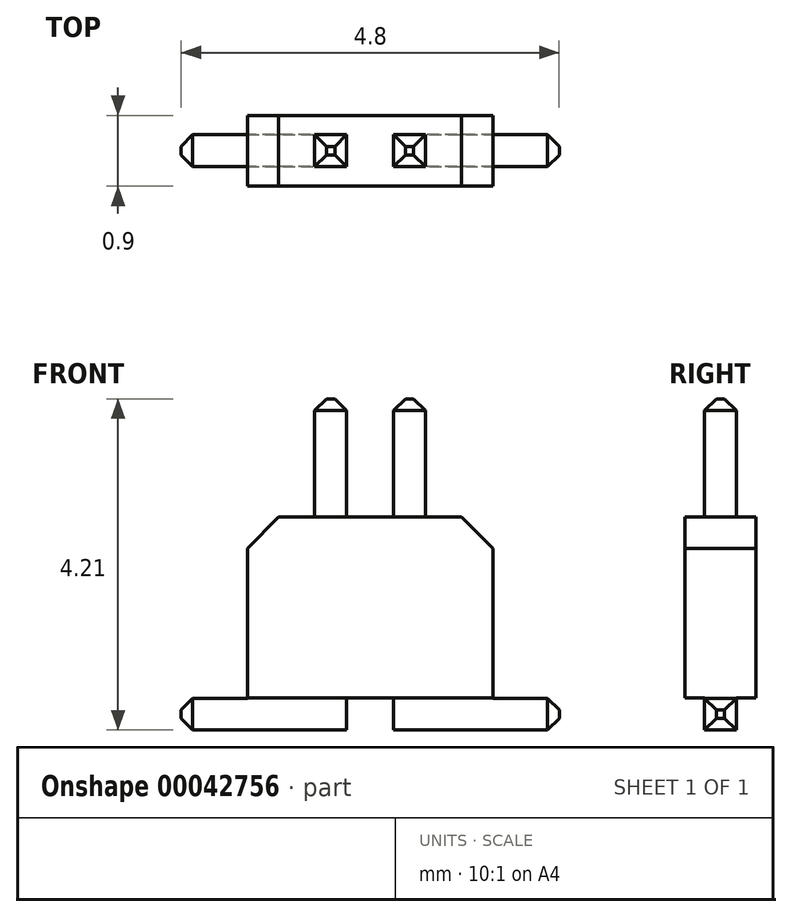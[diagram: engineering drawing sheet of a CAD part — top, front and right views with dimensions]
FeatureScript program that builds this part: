
annotation { "Feature Type Name" : "Feature", "Feature Type Description" : "" }
export const myFeature = defineFeature(function(context is Context, id is Id, definition is map)
    precondition{}
    {
        {
            var Q0;
            Q0=qCreatedBy(makeId("Top.planeOp"),FACE);
            var sketch = newSketch(context, id + "F0", { "sketchPlane" : qUnion([Q0])});
            skLineSegment(sketch, "E0.rect.bottom", {"start": v(-1.56, 0.45) * mm, "end": v(1.56, 0.45) * mm});
            skLineSegment(sketch, "E0.rect.top", {"start": v(-1.56, -0.45) * mm, "end": v(1.56, -0.45) * mm});
            skLineSegment(sketch, "E0.rect.left", {"start": v(-1.56, 0.45) * mm, "end": v(-1.56, -0.45) * mm});
            skLineSegment(sketch, "E0.rect.right", {"start": v(1.56, 0.45) * mm, "end": v(1.56, -0.45) * mm});
            skPoint(sketch, "E0.rect.middle", {"position": v(0, 0) * mm});
            skSolve(sketch);
        }
        {
            var Q0;
            Q0=qSketchRegion(id+"F0",true);
            extrude(context, id + "F1", {"entities" : qUnion([Q0]), "depth" : 2.3 * mm});
        }
        {
            var Q0;
            Q0=makeQuery(id+"F1.opExtrude","CAP_FACE",FACE,{"disambiguationData":[OSD([sQuery(id+"F0.wireOp",EDGE,"E0.rect.bottom"),sQuery(id+"F0.wireOp",EDGE,"E0.rect.top"),sQuery(id+"F0.wireOp",EDGE,"E0.rect.left"),sQuery(id+"F0.wireOp",EDGE,"E0.rect.right")])],"isStart":false});
            var sketch = newSketch(context, id + "F2", { "sketchPlane" : qUnion([Q0])});
            skLineSegment(sketch, "E1.rect.bottom", {"start": v(-0.7, -0.2) * mm, "end": v(-0.3, -0.2) * mm});
            skLineSegment(sketch, "E1.rect.top", {"start": v(-0.7, 0.2) * mm, "end": v(-0.3, 0.2) * mm});
            skLineSegment(sketch, "E1.rect.left", {"start": v(-0.7, -0.2) * mm, "end": v(-0.7, 0.2) * mm});
            skLineSegment(sketch, "E1.rect.right", {"start": v(-0.3, -0.2) * mm, "end": v(-0.3, 0.2) * mm});
            skPoint(sketch, "E1.rect.middle", {"position": v(-0.5, 0) * mm});
            skLineSegment(sketch, "E2.rect.bottom", {"start": v(0.7, 0.2) * mm, "end": v(0.3, 0.2) * mm});
            skLineSegment(sketch, "E2.rect.top", {"start": v(0.7, -0.2) * mm, "end": v(0.3, -0.2) * mm});
            skLineSegment(sketch, "E2.rect.left", {"start": v(0.7, 0.2) * mm, "end": v(0.7, -0.2) * mm});
            skLineSegment(sketch, "E2.rect.right", {"start": v(0.3, 0.2) * mm, "end": v(0.3, -0.2) * mm});
            skPoint(sketch, "E2.rect.middle", {"position": v(0.5, 0) * mm});
            skSolve(sketch);
        }
        {
            var Q0;
            Q0=qSketchRegion(id+"F2",true);
            extrude(context, id + "F3", {"entities" : qUnion([Q0]), "operationType" : NewBodyOperationType.ADD, "depth" : 1.5 * mm, "hasSecondDirection" : true, "secondDirectionOppositeDirection" : true, "secondDirectionDepth" : 2.7 * mm});
        }
        {
            var Q0;
            {var subQ0=sQuery(id+"F2.wireOp",EDGE,"E1.rect.left");Q0=makeQuery(id+"F3.boolean.opBoolean","SPLIT",FACE,{"disambiguationData":[TD([makeQuery(id+"F1.opExtrude","CAP_FACE",FACE,{"disambiguationData":[OSD([sQuery(id+"F0.wireOp",EDGE,"E0.rect.bottom"),sQuery(id+"F0.wireOp",EDGE,"E0.rect.top"),sQuery(id+"F0.wireOp",EDGE,"E0.rect.left"),sQuery(id+"F0.wireOp",EDGE,"E0.rect.right")])],"isStart":true})])],"derivedFrom":makeQuery(id+"F3.opExtrude","SWEPT_FACE",FACE,{"disambiguationData":[OSD([subQ0])]})});}
            var sketch = newSketch(context, id + "F4", { "sketchPlane" : qUnion([Q0])});
            skLineSegment(sketch, "E3.bottom", {"start": v(0.2, -0.41) * mm, "end": v(-0.2, -0.41) * mm});
            skLineSegment(sketch, "E3.top", {"start": v(0.2, 0) * mm, "end": v(-0.2, 0) * mm});
            skLineSegment(sketch, "E3.left", {"start": v(0.2, -0.41) * mm, "end": v(0.2, 0) * mm});
            skLineSegment(sketch, "E3.right", {"start": v(-0.2, -0.41) * mm, "end": v(-0.2, 0) * mm});
            skSolve(sketch);
        }
        {
            var Q0;
            Q0=qSketchRegion(id+"F4",true);
            extrude(context, id + "F5", {"entities" : qUnion([Q0]), "operationType" : NewBodyOperationType.ADD, "depth" : 1.7 * mm});
        }
        {
            var Q0;
            {var subQ0=sQuery(id+"F2.wireOp",EDGE,"E2.rect.left");Q0=makeQuery(id+"F3.boolean.opBoolean","SPLIT",FACE,{"disambiguationData":[TD([makeQuery(id+"F1.opExtrude","CAP_FACE",FACE,{"disambiguationData":[OSD([sQuery(id+"F0.wireOp",EDGE,"E0.rect.bottom"),sQuery(id+"F0.wireOp",EDGE,"E0.rect.top"),sQuery(id+"F0.wireOp",EDGE,"E0.rect.left"),sQuery(id+"F0.wireOp",EDGE,"E0.rect.right")])],"isStart":true})])],"derivedFrom":makeQuery(id+"F3.opExtrude","SWEPT_FACE",FACE,{"disambiguationData":[OSD([subQ0])]})});}
            var sketch = newSketch(context, id + "F6", { "sketchPlane" : qUnion([Q0])});
            skLineSegment(sketch, "E4.bottom", {"start": v(0.2, -0.41) * mm, "end": v(-0.2, -0.41) * mm});
            skLineSegment(sketch, "E4.top", {"start": v(0.2, 0) * mm, "end": v(-0.2, 0) * mm});
            skLineSegment(sketch, "E4.left", {"start": v(0.2, -0.41) * mm, "end": v(0.2, 0) * mm});
            skLineSegment(sketch, "E4.right", {"start": v(-0.2, -0.41) * mm, "end": v(-0.2, 0) * mm});
            skSolve(sketch);
        }
        {
            var Q0;
            Q0=qSketchRegion(id+"F6",true);
            extrude(context, id + "F7", {"entities" : qUnion([Q0]), "operationType" : NewBodyOperationType.ADD, "depth" : 1.7 * mm});
        }
        {
            var Q0;
            Q0=makeQuery(id+"F1.opExtrude","CAP_EDGE",EDGE,{"disambiguationData":[OSD([sQuery(id+"F0.wireOp",EDGE,"E0.rect.right")])],"isStart":false});
            var Q1;
            Q1=makeQuery(id+"F1.opExtrude","CAP_EDGE",EDGE,{"disambiguationData":[OSD([sQuery(id+"F0.wireOp",EDGE,"E0.rect.left")])],"isStart":false});
            chamfer(context, id + "F8", {"entities" : qUnion([Q0, Q1]), "width" : .4 * mm, "tangentPropagation" : true});
        }
        {
            var Q0;
            Q0=makeQuery(id+"F3.opExtrude","CAP_EDGE",EDGE,{"disambiguationData":[OSD([sQuery(id+"F2.wireOp",EDGE,"E1.rect.top")])],"isStart":false});
            var Q1;
            Q1=makeQuery(id+"F3.opExtrude","CAP_EDGE",EDGE,{"disambiguationData":[OSD([sQuery(id+"F2.wireOp",EDGE,"E2.rect.bottom")])],"isStart":false});
            var Q2;
            Q2=makeQuery(id+"F3.opExtrude","CAP_EDGE",EDGE,{"disambiguationData":[OSD([sQuery(id+"F2.wireOp",EDGE,"E2.rect.left")])],"isStart":false});
            var Q3;
            Q3=makeQuery(id+"F3.opExtrude","CAP_EDGE",EDGE,{"disambiguationData":[OSD([sQuery(id+"F2.wireOp",EDGE,"E2.rect.top")])],"isStart":false});
            var Q4;
            Q4=makeQuery(id+"F3.opExtrude","CAP_EDGE",EDGE,{"disambiguationData":[OSD([sQuery(id+"F2.wireOp",EDGE,"E2.rect.right")])],"isStart":false});
            var Q5;
            Q5=makeQuery(id+"F3.opExtrude","CAP_EDGE",EDGE,{"disambiguationData":[OSD([sQuery(id+"F2.wireOp",EDGE,"E1.rect.right")])],"isStart":false});
            var Q6;
            Q6=makeQuery(id+"F3.opExtrude","CAP_EDGE",EDGE,{"disambiguationData":[OSD([sQuery(id+"F2.wireOp",EDGE,"E1.rect.bottom")])],"isStart":false});
            var Q7;
            Q7=makeQuery(id+"F3.opExtrude","CAP_EDGE",EDGE,{"disambiguationData":[OSD([sQuery(id+"F2.wireOp",EDGE,"E1.rect.left")])],"isStart":false});
            var Q8;
            Q8=makeQuery(id+"F5.opExtrude","CAP_EDGE",EDGE,{"disambiguationData":[OSD([sQuery(id+"F4.wireOp",EDGE,"E3.top")])],"isStart":false});
            var Q9;
            Q9=makeQuery(id+"F5.opExtrude","CAP_EDGE",EDGE,{"disambiguationData":[OSD([sQuery(id+"F4.wireOp",EDGE,"E3.right")])],"isStart":false});
            var Q10;
            Q10=makeQuery(id+"F5.opExtrude","CAP_EDGE",EDGE,{"disambiguationData":[OSD([sQuery(id+"F4.wireOp",EDGE,"E3.bottom")])],"isStart":false});
            var Q11;
            Q11=makeQuery(id+"F5.opExtrude","CAP_EDGE",EDGE,{"disambiguationData":[OSD([sQuery(id+"F4.wireOp",EDGE,"E3.left")])],"isStart":false});
            var Q12;
            Q12=makeQuery(id+"F7.opExtrude","CAP_EDGE",EDGE,{"disambiguationData":[OSD([sQuery(id+"F6.wireOp",EDGE,"E4.top")])],"isStart":false});
            var Q13;
            Q13=makeQuery(id+"F7.opExtrude","CAP_EDGE",EDGE,{"disambiguationData":[OSD([sQuery(id+"F6.wireOp",EDGE,"E4.left")])],"isStart":false});
            var Q14;
            Q14=makeQuery(id+"F7.opExtrude","CAP_EDGE",EDGE,{"disambiguationData":[OSD([sQuery(id+"F6.wireOp",EDGE,"E4.bottom")])],"isStart":false});
            var Q15;
            Q15=makeQuery(id+"F7.opExtrude","CAP_EDGE",EDGE,{"disambiguationData":[OSD([sQuery(id+"F6.wireOp",EDGE,"E4.right")])],"isStart":false});
            chamfer(context, id + "F9", {"entities" : qUnion([Q0, Q1, Q2, Q3, Q4, Q5, Q6, Q7, Q8, Q9, Q10, Q11, Q12, Q13, Q14, Q15]), "width" : .15 * mm, "tangentPropagation" : true});
        }
    });
